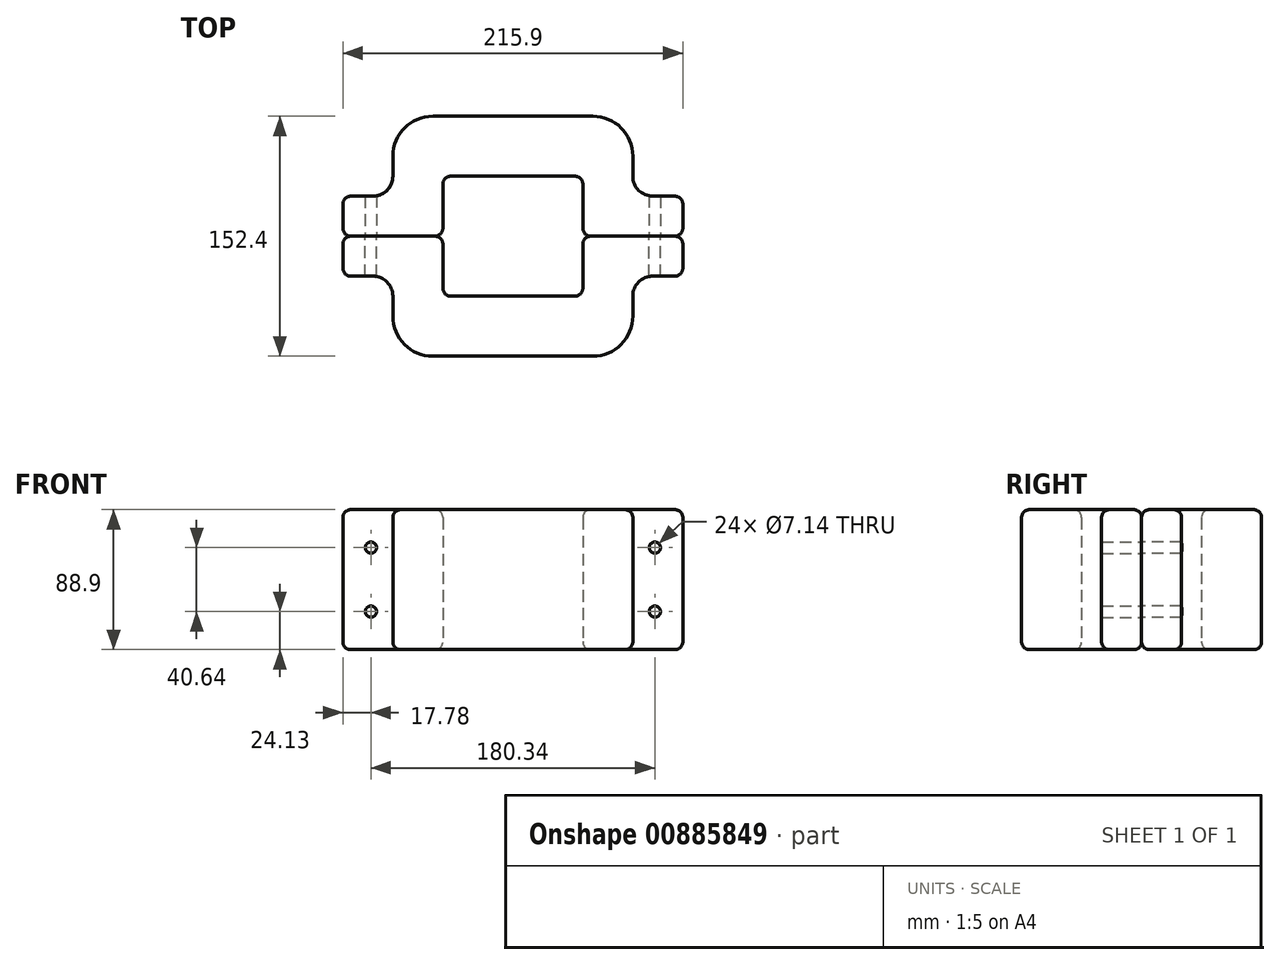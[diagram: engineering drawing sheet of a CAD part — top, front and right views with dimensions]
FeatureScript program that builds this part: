
annotation { "Feature Type Name" : "Feature", "Feature Type Description" : "" }
export const myFeature = defineFeature(function(context is Context, id is Id, definition is map)
    precondition{}
    {
        {
            var Q0;
            Q0=qCreatedBy(makeId("Top.planeOp"),FACE);
            var sketch = newSketch(context, id + "F0", { "sketchPlane" : qUnion([Q0])});
            skLineSegment(sketch, "E0.bottom", {"start": v(76.2, 51) * mm, "end": v(-76.2, 51) * mm});
            skLineSegment(sketch, "E0.left", {"start": v(76.2, 51) * mm, "end": v(76.2, 0.2) * mm});
            skLineSegment(sketch, "E0.right", {"start": v(-76.2, 51) * mm, "end": v(-76.2, 0.2) * mm});
            skPoint(sketch, "E0.middle", {"position": v(0, 0) * mm});
            skLineSegment(sketch, "E1", {"start": v(-76.2, 0.2) * mm, "end": v(-107.95, 0.2) * mm});
            skLineSegment(sketch, "E2", {"start": v(76.2, 0.2) * mm, "end": v(107.95, 0.2) * mm});
            skPoint(sketch, "E3.end.orphan", {"position": v(-76.2, -51) * mm});
            skPoint(sketch, "E4.start.orphan", {"position": v(66.84, -51) * mm});
            skPoint(sketch, "E5.end.orphan", {"position": v(76.2, -51) * mm});
            skPoint(sketch, "E6.end.orphan", {"position": v(-101.6, -51) * mm});
            skPoint(sketch, "E7.end.orphan", {"position": v(101.6, -51) * mm});
            skLineSegment(sketch, "E8", {"start": v(-107.95, 0.2) * mm, "end": v(-107.95, -25.2) * mm});
            skLineSegment(sketch, "E9", {"start": v(-107.95, -25.2) * mm, "end": v(-44.45, -25.2) * mm});
            skLineSegment(sketch, "E10", {"start": v(107.95, -25.2) * mm, "end": v(107.95, 0.2) * mm});
            skLineSegment(sketch, "E11", {"start": v(-44.45, -25.2) * mm, "end": v(-44.45, 12.9) * mm});
            skLineSegment(sketch, "E12", {"start": v(-44.45, 12.9) * mm, "end": v(44.45, 12.9) * mm});
            skLineSegment(sketch, "E13", {"start": v(44.45, 12.9) * mm, "end": v(44.45, -25.2) * mm});
            skLineSegment(sketch, "E14.trimOffspring", {"start": v(44.45, -25.2) * mm, "end": v(107.95, -25.2) * mm});
            skSolve(sketch);
        }
        {
            var Q0;
            Q0 = qSketchRegion(id + "F0", true);
            extrude(context, id + "F1", {"entities" : qUnion([Q0]), "depth" : 88.9 * mm, "offsetDistance" : 25.4 * mm});
        }
        {
            var Q0;
            Q0=makeQuery(id+"F1.opExtrude","SWEPT_EDGE",EDGE,{"disambiguationData":[OSD([sQuery(id+"F0.wireOp",EDGE,"E0.right"),sQuery(id+"F0.wireOp",EDGE,"E1")])]});
            var Q1;
            Q1=makeQuery(id+"F1.opExtrude","SWEPT_EDGE",EDGE,{"disambiguationData":[OSD([sQuery(id+"F0.wireOp",EDGE,"E0.left"),sQuery(id+"F0.wireOp",EDGE,"E2")])]});
            fillet(context, id + "F2", {"entities" : qUnion([Q0, Q1]), "radius" : 12.7 * mm, "tangentPropagation" : true, "allowEdgeOverflow" : false});
        }
        {
            var Q0;
            Q0=makeQuery(id+"F1.opExtrude","SWEPT_EDGE",EDGE,{"disambiguationData":[OSD([sQuery(id+"F0.wireOp",EDGE,"E0.bottom"),sQuery(id+"F0.wireOp",EDGE,"E0.left")])]});
            var Q1;
            Q1=makeQuery(id+"F1.opExtrude","SWEPT_EDGE",EDGE,{"disambiguationData":[OSD([sQuery(id+"F0.wireOp",EDGE,"E0.bottom"),sQuery(id+"F0.wireOp",EDGE,"E0.right")])]});
            fillet(context, id + "F3", {"entities" : qUnion([Q0, Q1]), "radius" : 25.4 * mm, "tangentPropagation" : true, "allowEdgeOverflow" : false});
        }
        {
            var Q0;
            Q0=makeQuery(id+"F1.opExtrude","SWEPT_EDGE",EDGE,{"disambiguationData":[OSD([sQuery(id+"F0.wireOp",EDGE,"E12"),sQuery(id+"F0.wireOp",EDGE,"E13")])]});
            var Q1;
            Q1=makeQuery(id+"F1.opExtrude","SWEPT_EDGE",EDGE,{"disambiguationData":[OSD([sQuery(id+"F0.wireOp",EDGE,"E11"),sQuery(id+"F0.wireOp",EDGE,"E12")])]});
            var Q2;
            Q2=makeQuery(id+"F1.opExtrude","SWEPT_FACE",FACE,{"disambiguationData":[OSD([sQuery(id+"F0.wireOp",EDGE,"E8")])]});
            var Q3;
            Q3=makeQuery(id+"F1.opExtrude","SWEPT_FACE",FACE,{"disambiguationData":[OSD([sQuery(id+"F0.wireOp",EDGE,"E10")])]});
            var Q4;
            Q4=makeQuery(id+"F1.opExtrude","CAP_FACE",FACE,{"disambiguationData":[OSD([sQuery(id+"F0.wireOp",EDGE,"E0.bottom"),sQuery(id+"F0.wireOp",EDGE,"E0.left"),sQuery(id+"F0.wireOp",EDGE,"E0.right"),sQuery(id+"F0.wireOp",EDGE,"E1"),sQuery(id+"F0.wireOp",EDGE,"E2"),sQuery(id+"F0.wireOp",EDGE,"E8"),sQuery(id+"F0.wireOp",EDGE,"E9"),sQuery(id+"F0.wireOp",EDGE,"E10"),sQuery(id+"F0.wireOp",EDGE,"E11"),sQuery(id+"F0.wireOp",EDGE,"E12"),sQuery(id+"F0.wireOp",EDGE,"E13"),sQuery(id+"F0.wireOp",EDGE,"E14.trimOffspring")])],"isStart":false});
            var Q5;
            Q5=makeQuery(id+"F1.opExtrude","CAP_FACE",FACE,{"disambiguationData":[OSD([sQuery(id+"F0.wireOp",EDGE,"E0.bottom"),sQuery(id+"F0.wireOp",EDGE,"E0.left"),sQuery(id+"F0.wireOp",EDGE,"E0.right"),sQuery(id+"F0.wireOp",EDGE,"E1"),sQuery(id+"F0.wireOp",EDGE,"E2"),sQuery(id+"F0.wireOp",EDGE,"E8"),sQuery(id+"F0.wireOp",EDGE,"E9"),sQuery(id+"F0.wireOp",EDGE,"E10"),sQuery(id+"F0.wireOp",EDGE,"E11"),sQuery(id+"F0.wireOp",EDGE,"E12"),sQuery(id+"F0.wireOp",EDGE,"E13"),sQuery(id+"F0.wireOp",EDGE,"E14.trimOffspring")])],"isStart":true});
            var Q6;
            Q6=makeQuery(id+"F1.opExtrude","SWEPT_EDGE",EDGE,{"disambiguationData":[OSD([sQuery(id+"F0.wireOp",EDGE,"E9"),sQuery(id+"F0.wireOp",EDGE,"E11")])]});
            var Q7;
            Q7=makeQuery(id+"F1.opExtrude","SWEPT_EDGE",EDGE,{"disambiguationData":[OSD([sQuery(id+"F0.wireOp",EDGE,"E13"),sQuery(id+"F0.wireOp",EDGE,"E14.trimOffspring")])]});
            fillet(context, id + "F4", {"entities" : qUnion([Q0, Q1, Q2, Q3, Q4, Q5, Q6, Q7]), "radius" : 5.08 * mm, "tangentPropagation" : true, "allowEdgeOverflow" : false});
        }
        {
            var Q0;
            Q0=makeQuery(id+"F1.opExtrude","SWEPT_FACE",FACE,{"disambiguationData":[OSD([sQuery(id+"F0.wireOp",EDGE,"E9")])]});
            var sketch = newSketch(context, id + "F5", { "sketchPlane" : qUnion([Q0])});
            skPoint(sketch, "E15", {"position": v(-90.17, 64.77) * mm});
            skPoint(sketch, "E16", {"position": v(-90.17, 24.13) * mm});
            skPoint(sketch, "E17", {"position": v(90.17, 64.77) * mm});
            skPoint(sketch, "E18", {"position": v(90.17, 24.13) * mm});
            skSolve(sketch);
        }
        {
            var Q0;
            Q0=sQuery(id+"F5.wireOp",VERTEX,"E15");
            var Q1;
            Q1=sQuery(id+"F5.wireOp",VERTEX,"E16");
            var Q2;
            Q2=sQuery(id+"F5.wireOp",VERTEX,"E17");
            var Q3;
            Q3=sQuery(id+"F5.wireOp",VERTEX,"E18");
            var Q4;
            Q4=makeQuery(id+"F1.opExtrude","SWEPT_BODY",BODY,{"disambiguationData":[OSD([sQuery(id+"F0.wireOp",EDGE,"E0.bottom"),sQuery(id+"F0.wireOp",EDGE,"E0.left"),sQuery(id+"F0.wireOp",EDGE,"E0.right"),sQuery(id+"F0.wireOp",EDGE,"E1"),sQuery(id+"F0.wireOp",EDGE,"E2"),sQuery(id+"F0.wireOp",EDGE,"E8"),sQuery(id+"F0.wireOp",EDGE,"E9"),sQuery(id+"F0.wireOp",EDGE,"E10"),sQuery(id+"F0.wireOp",EDGE,"E11"),sQuery(id+"F0.wireOp",EDGE,"E12"),sQuery(id+"F0.wireOp",EDGE,"E13"),sQuery(id+"F0.wireOp",EDGE,"E14.trimOffspring")])]});
            hole(context, id + "F6", {"style" : HoleStyle.SIMPLE, "endStyle" : HoleEndStyle.THROUGH, "holeDiameter" : 7.14 * mm, "majorDiameter" : 6.35 * mm, "isTappedThrough" : true, "tappedDepth" : 12.7 * mm, "tapClearance" : 3, "locations" : qUnion([Q0, Q1, Q2, Q3]), "scope" : qUnion([Q4])});
        }
        {
            var Q0;
            Q0=makeQuery(id+"F1.opExtrude","SWEPT_BODY",BODY,{"disambiguationData":[OSD([sQuery(id+"F0.wireOp",EDGE,"E0.bottom"),sQuery(id+"F0.wireOp",EDGE,"E0.left"),sQuery(id+"F0.wireOp",EDGE,"E0.right"),sQuery(id+"F0.wireOp",EDGE,"E1"),sQuery(id+"F0.wireOp",EDGE,"E2"),sQuery(id+"F0.wireOp",EDGE,"E8"),sQuery(id+"F0.wireOp",EDGE,"E9"),sQuery(id+"F0.wireOp",EDGE,"E10"),sQuery(id+"F0.wireOp",EDGE,"E11"),sQuery(id+"F0.wireOp",EDGE,"E12"),sQuery(id+"F0.wireOp",EDGE,"E13"),sQuery(id+"F0.wireOp",EDGE,"E14.trimOffspring")])]});
            var Q1;
            Q1=makeQuery(id+"F1.opExtrude","SWEPT_FACE",FACE,{"disambiguationData":[OSD([sQuery(id+"F0.wireOp",EDGE,"E9")])]});
            mirror(context, id + "F7", {"entities" : qUnion([Q0]), "mirrorPlane" : qUnion([Q1])});
        }
    });
